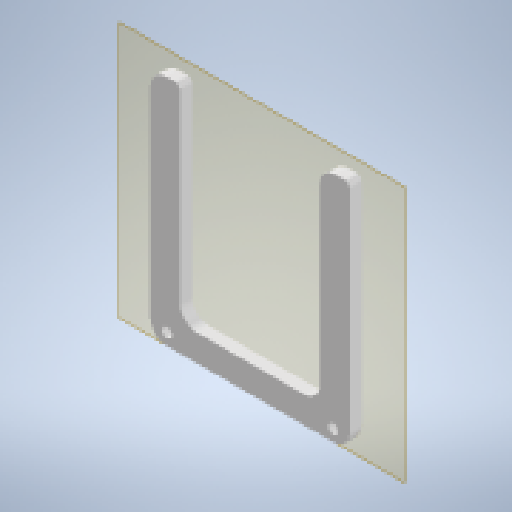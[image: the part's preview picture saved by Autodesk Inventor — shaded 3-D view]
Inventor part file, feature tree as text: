
AUTODESK INVENTOR PART (.ipt)
format: ipt  version: 2024.2 (Build 282272000, 272)  size: 167,936 bytes
history: native  units: mm
features: other x13, extrude x1, sketch x1, reference x1
ambient origin geometry x8: Origin, YZ Plane, XZ Plane, XY Plane, X Axis, Y Axis, Z Axis, Center Point
bodies: Body1 (feature_tree)
feature tree (16):
  other  "Твердое тело1"
  other  "РабПлоскость1"
  extrude  "Выдавливание1"  Depth=5.0mm
  other  "Сопряжение грани1"
  other  "Сопряжение грани2"
  other  "Сопряжение грани3"
  other  "Сопряжение грани4"
  other  "Сопряжение грани5"
  other  "Сопряжение грани6"
  other  "Сопряжение грани7"
  other  "Сопряжение грани8"
  sketch  "Эскиз1"
  reference  "Ссылка1"
  other  "<userpath>\Documents\Artist\3D\каретка.iam"
  other  "каретка.iam"
  other  "ANY:13"
